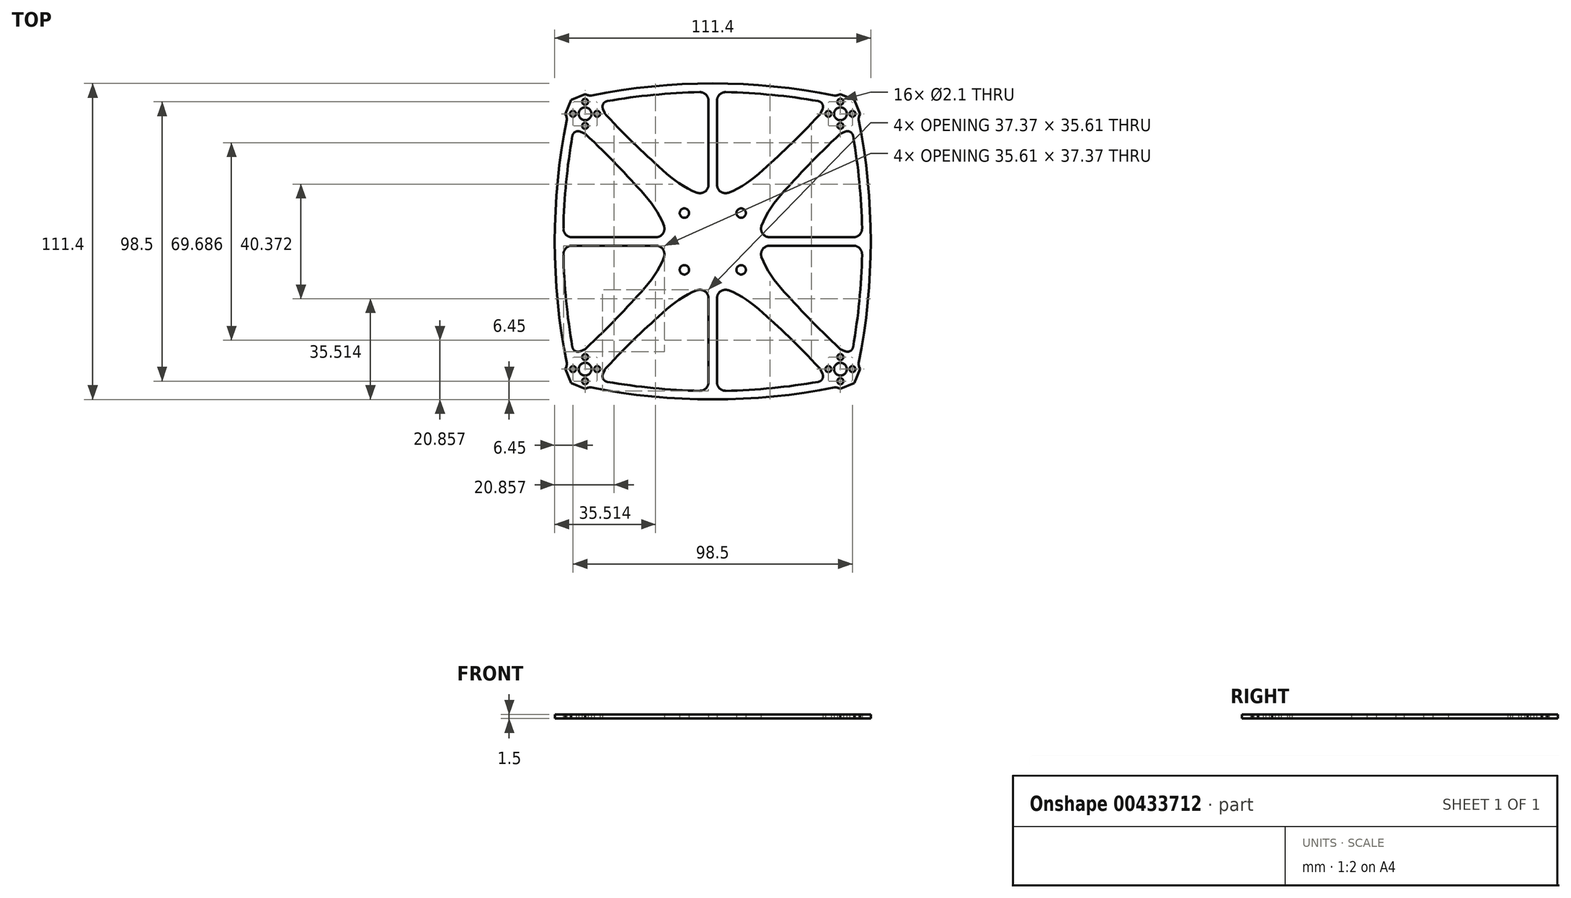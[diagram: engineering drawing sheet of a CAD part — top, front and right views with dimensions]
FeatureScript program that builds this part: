
annotation { "Feature Type Name" : "Feature", "Feature Type Description" : "" }
export const myFeature = defineFeature(function(context is Context, id is Id, definition is map)
    precondition{}
    {
        {
            var Q0;
            Q0=qCreatedBy(makeId("Top.planeOp"),FACE);
            var sketch = newSketch(context, id + "F0", { "sketchPlane" : qUnion([Q0])});
            skLineSegment(sketch, "E0.bottom", {"start": v(45, 45) * mm, "end": v(-45, 45) * mm, "construction": true});
            skLineSegment(sketch, "E0.top", {"start": v(45, -45) * mm, "end": v(-45, -45) * mm, "construction": true});
            skLineSegment(sketch, "E0.left", {"start": v(45, 45) * mm, "end": v(45, -45) * mm, "construction": true});
            skLineSegment(sketch, "E0.right", {"start": v(-45, 45) * mm, "end": v(-45, -45) * mm, "construction": true});
            skPoint(sketch, "E0.middle", {"position": v(0, 0) * mm});
            skLineSegment(sketch, "E1.bottom", {"start": v(10, -10) * mm, "end": v(-10, -10) * mm, "construction": true});
            skLineSegment(sketch, "E1.top", {"start": v(10, 10) * mm, "end": v(-10, 10) * mm, "construction": true});
            skLineSegment(sketch, "E1.left", {"start": v(10, -10) * mm, "end": v(10, 10) * mm, "construction": true});
            skLineSegment(sketch, "E1.right", {"start": v(-10, -10) * mm, "end": v(-10, 10) * mm, "construction": true});
            skCircle(sketch, "E2", {"center": v(45, 45) * mm, "radius": 4.25 * mm, "construction": true});
            skLineSegment(sketch, "E3", {"start": v(-45, 0) * mm, "end": v(45, 0) * mm, "construction": true});
            skLineSegment(sketch, "E4", {"start": v(0, 45) * mm, "end": v(0, -45) * mm, "construction": true});
            skLineSegment(sketch, "E5", {"start": v(0, 0) * mm, "end": v(45, 45) * mm, "construction": true});
            skCircle(sketch, "E6", {"center": v(45, 40.75) * mm, "radius": 1.05 * mm, "construction": true});
            skLineSegment(sketch, "E7", {"start": v(45, 45) * mm, "end": v(56.69, 33.31) * mm, "construction": true});
            skCircle(sketch, "E8.MirrorC", {"center": v(40.75, 45) * mm, "radius": 1.05 * mm, "construction": true});
            skCircle(sketch, "E9.MirrorC", {"center": v(49.25, 45) * mm, "radius": 1.05 * mm, "construction": true});
            skCircle(sketch, "E10.MirrorC", {"center": v(45, 49.25) * mm, "radius": 1.05 * mm, "construction": true});
            skCircle(sketch, "E11", {"center": v(45, 45) * mm, "radius": 6.8 * mm, "construction": true});
            skCircle(sketch, "E12.MirrorC", {"center": v(40.75, -45) * mm, "radius": 1.05 * mm, "construction": true});
            skCircle(sketch, "E13.MirrorC", {"center": v(45, -49.25) * mm, "radius": 1.05 * mm, "construction": true});
            skCircle(sketch, "E14.MirrorC", {"center": v(45, -40.75) * mm, "radius": 1.05 * mm, "construction": true});
            skCircle(sketch, "E15.MirrorC", {"center": v(45, -45) * mm, "radius": 4.25 * mm, "construction": true});
            skCircle(sketch, "E16.MirrorC", {"center": v(49.25, -45) * mm, "radius": 1.05 * mm, "construction": true});
            skCircle(sketch, "E17.MirrorC", {"center": v(45, -45) * mm, "radius": 6.8 * mm, "construction": true});
            skCircle(sketch, "E18.MirrorC", {"center": v(-45, 49.25) * mm, "radius": 1.05 * mm, "construction": true});
            skCircle(sketch, "E19.MirrorC", {"center": v(-45, -49.25) * mm, "radius": 1.05 * mm, "construction": true});
            skCircle(sketch, "E20.MirrorC", {"center": v(-45, -40.75) * mm, "radius": 1.05 * mm, "construction": true});
            skCircle(sketch, "E21.MirrorC", {"center": v(-49.25, -45) * mm, "radius": 1.05 * mm, "construction": true});
            skCircle(sketch, "E22.MirrorC", {"center": v(-49.25, 45) * mm, "radius": 1.05 * mm, "construction": true});
            skCircle(sketch, "E23.MirrorC", {"center": v(-40.75, 45) * mm, "radius": 1.05 * mm, "construction": true});
            skCircle(sketch, "E24.MirrorC", {"center": v(-40.75, -45) * mm, "radius": 1.05 * mm, "construction": true});
            skCircle(sketch, "E25.MirrorC", {"center": v(-45, 40.75) * mm, "radius": 1.05 * mm, "construction": true});
            skCircle(sketch, "E26.MirrorC", {"center": v(-45, -45) * mm, "radius": 4.25 * mm, "construction": true});
            skCircle(sketch, "E27.MirrorC", {"center": v(-45, 45) * mm, "radius": 6.8 * mm, "construction": true});
            skCircle(sketch, "E28.MirrorC", {"center": v(-45, -45) * mm, "radius": 6.8 * mm, "construction": true});
            skCircle(sketch, "E29.MirrorC", {"center": v(-45, 45) * mm, "radius": 4.25 * mm, "construction": true});
            skSolve(sketch);
        }
        {
            var Q0;
            Q0=qCreatedBy(makeId("Top.planeOp"),FACE);
            var sketch = newSketch(context, id + "F1", { "sketchPlane" : qUnion([Q0])});
            skCircle(sketch, "E30", {"center": v(10, 10) * mm, "radius": 1.65 * mm});
            skCircle(sketch, "E31", {"center": v(40.75, 45) * mm, "radius": 1.05 * mm});
            skCircle(sketch, "E32.MirrorC", {"center": v(45, 40.75) * mm, "radius": 1.05 * mm});
            skCircle(sketch, "E33.MirrorC", {"center": v(49.25, 45) * mm, "radius": 1.05 * mm});
            skCircle(sketch, "E34.MirrorC", {"center": v(45, 49.25) * mm, "radius": 1.05 * mm});
            skCircle(sketch, "E35", {"center": v(45, 45) * mm, "radius": 2.25 * mm});
            skCircle(sketch, "E36.cCircle", {"center": v(45, 45) * mm, "radius": 6.47 * mm, "construction": true});
            skLineSegment(sketch, "E36.0", {"start": v(52, 45) * mm, "end": v(51.6, 44.02) * mm});
            skLineSegment(sketch, "E36.1", {"start": v(47.47, 39.03) * mm, "end": v(45, 38) * mm});
            skLineSegment(sketch, "E36.4", {"start": v(38.14, 45.34) * mm, "end": v(38.72, 46.74) * mm});
            skLineSegment(sketch, "E36.5", {"start": v(44.02, 51.6) * mm, "end": v(45, 52) * mm});
            skLineSegment(sketch, "E36.6", {"start": v(45, 52) * mm, "end": v(49.95, 49.95) * mm});
            skLineSegment(sketch, "E36.7", {"start": v(49.95, 49.95) * mm, "end": v(52, 45) * mm});
            skPoint(sketch, "E36.0.midPoint", {"position": v(50.97, 42.53) * mm});
            skFitSpline(sketch, "E37", {"points": [v(38, 45) * mm, v(19.97, 27.24) * mm, v(0, 16.2) * mm], "startDerivative": vector(-40.7, -43.47) * mm, "endDerivative": vector(-49.26, -1.01) * mm});
            skLineSegment(sketch, "E38", {"start": v(0, 16.2) * mm, "end": v(-10.4, 16.2) * mm, "construction": true});
            skFitSpline(sketch, "E39.MirrorCS", {"points": [v(45, 38) * mm, v(27.24, 19.97) * mm, v(16.2, 0) * mm], "startDerivative": vector(-43.47, -40.7) * mm, "endDerivative": vector(-1.01, -49.26) * mm});
            skArc(sketch, "E40", {"start": v(49.95, 49.95) * mm, "mid": v(49.4, 50.08) * mm, "end": v(48.84, 50.2) * mm});
            skArc(sketch, "E41.0", {"start": v(37.22, 49.48) * mm, "mid": v(20.95, 51.68) * mm, "end": v(4.56, 52.65) * mm});
            skLineSegment(sketch, "E42", {"start": v(0, 55.7) * mm, "end": v(-9.83, 55.7) * mm, "construction": true});
            skArc(sketch, "E43.trimOffspring", {"start": v(42.86, 51.48) * mm, "mid": v(21.53, 54.64) * mm, "end": v(0, 55.7) * mm});
            skPoint(sketch, "E44.orphan", {"position": v(40.05, 49.95) * mm});
            skPoint(sketch, "E45.visualSharp", {"position": v(39.67, 49.04) * mm});
            skArc(sketch, "E45.filletArc", {"start": v(38.72, 46.74) * mm, "mid": v(38.63, 48.47) * mm, "end": v(37.22, 49.48) * mm});
            skPoint(sketch, "E46.visualSharp", {"position": v(43.46, 51.36) * mm});
            skArc(sketch, "E46.filletArc", {"start": v(42.86, 51.48) * mm, "mid": v(43.45, 51.45) * mm, "end": v(44.02, 51.6) * mm});
            skArc(sketch, "E47.filletArc", {"start": v(37.75, 44.73) * mm, "mid": v(37.97, 45.02) * mm, "end": v(38.14, 45.34) * mm});
            skArc(sketch, "E48.MirrorCS", {"start": v(49.48, 37.22) * mm, "mid": v(51.68, 20.95) * mm, "end": v(52.65, 4.56) * mm});
            skArc(sketch, "E49.MirrorCS", {"start": v(51.48, 42.86) * mm, "mid": v(54.64, 21.53) * mm, "end": v(55.7, 0) * mm});
            skArc(sketch, "E50.MirrorCS", {"start": v(46.74, 38.72) * mm, "mid": v(48.47, 38.63) * mm, "end": v(49.48, 37.22) * mm});
            skArc(sketch, "E51.MirrorCS", {"start": v(51.48, 42.86) * mm, "mid": v(51.45, 43.45) * mm, "end": v(51.6, 44.02) * mm});
            skPoint(sketch, "E52.orphan", {"position": v(49.95, 40.05) * mm});
            skLineSegment(sketch, "E53", {"start": v(1.5, 49.65) * mm, "end": v(1.5, 20.03) * mm});
            skPoint(sketch, "E54.orphan", {"position": v(0, 52.7) * mm});
            skPoint(sketch, "E55.visualSharp", {"position": v(1.5, 16.3) * mm});
            skArc(sketch, "E55.filletArc", {"start": v(1.5, 20.03) * mm, "mid": v(2.75, 17.59) * mm, "end": v(5.46, 17.19) * mm});
            skPoint(sketch, "E56.visualSharp", {"position": v(1.5, 52.69) * mm});
            skArc(sketch, "E56.filletArc", {"start": v(4.56, 52.65) * mm, "mid": v(2.4, 51.8) * mm, "end": v(1.5, 49.65) * mm});
            skLineSegment(sketch, "E57.MirrorCS", {"start": v(49.65, 1.5) * mm, "end": v(20.03, 1.5) * mm});
            skArc(sketch, "E58.MirrorCS", {"start": v(20.03, 1.5) * mm, "mid": v(17.59, 2.75) * mm, "end": v(17.19, 5.46) * mm});
            skArc(sketch, "E59.MirrorCS", {"start": v(52.65, 4.56) * mm, "mid": v(51.8, 2.4) * mm, "end": v(49.65, 1.5) * mm});
            skPoint(sketch, "E60.orphan", {"position": v(52.7, 0) * mm});
            skArc(sketch, "E61.MirrorCS", {"start": v(37.75, -44.73) * mm, "mid": v(37.97, -45.02) * mm, "end": v(38.14, -45.34) * mm});
            skLineSegment(sketch, "E62.MirrorCS", {"start": v(38.14, -45.34) * mm, "end": v(38.72, -46.74) * mm});
            skCircle(sketch, "E63.MirrorC", {"center": v(45, -40.75) * mm, "radius": 1.05 * mm});
            skArc(sketch, "E64.MirrorCS", {"start": v(49.95, -49.95) * mm, "mid": v(49.4, -50.08) * mm, "end": v(48.84, -50.2) * mm});
            skLineSegment(sketch, "E65.MirrorCS", {"start": v(44.02, -51.6) * mm, "end": v(45, -52) * mm});
            skLineSegment(sketch, "E66.MirrorCS", {"start": v(45, -52) * mm, "end": v(49.95, -49.95) * mm});
            skLineSegment(sketch, "E67.MirrorCS", {"start": v(47.47, -39.03) * mm, "end": v(45, -38) * mm});
            skArc(sketch, "E68.MirrorCS", {"start": v(51.48, -42.86) * mm, "mid": v(51.45, -43.45) * mm, "end": v(51.6, -44.02) * mm});
            skArc(sketch, "E69.MirrorCS", {"start": v(42.86, -51.48) * mm, "mid": v(43.45, -51.45) * mm, "end": v(44.02, -51.6) * mm});
            skLineSegment(sketch, "E70.MirrorCS", {"start": v(52, -45) * mm, "end": v(51.6, -44.02) * mm});
            skArc(sketch, "E71.MirrorCS", {"start": v(38.72, -46.74) * mm, "mid": v(38.63, -48.47) * mm, "end": v(37.22, -49.48) * mm});
            skArc(sketch, "E72.MirrorCS", {"start": v(4.56, -52.65) * mm, "mid": v(2.4, -51.8) * mm, "end": v(1.5, -49.65) * mm});
            skArc(sketch, "E73.MirrorCS", {"start": v(46.74, -38.72) * mm, "mid": v(48.47, -38.63) * mm, "end": v(49.48, -37.22) * mm});
            skArc(sketch, "E74.MirrorCS", {"start": v(52.65, -4.56) * mm, "mid": v(51.8, -2.4) * mm, "end": v(49.65, -1.5) * mm});
            skCircle(sketch, "E75.MirrorC", {"center": v(40.75, -45) * mm, "radius": 1.05 * mm});
            skPoint(sketch, "E76.MirrorP", {"position": v(38, -45) * mm});
            skCircle(sketch, "E77.MirrorC", {"center": v(49.25, -45) * mm, "radius": 1.05 * mm});
            skArc(sketch, "E78.MirrorCS", {"start": v(1.5, -20.03) * mm, "mid": v(2.75, -17.59) * mm, "end": v(5.46, -17.19) * mm});
            skCircle(sketch, "E79.MirrorC", {"center": v(45, -45) * mm, "radius": 2.25 * mm});
            skCircle(sketch, "E80.MirrorC", {"center": v(45, -49.25) * mm, "radius": 1.05 * mm});
            skArc(sketch, "E81.MirrorCS", {"start": v(20.03, -1.5) * mm, "mid": v(17.59, -2.75) * mm, "end": v(17.19, -5.46) * mm});
            skCircle(sketch, "E82.MirrorC", {"center": v(10, -10) * mm, "radius": 1.65 * mm});
            skLineSegment(sketch, "E83.MirrorCS", {"start": v(49.95, -49.95) * mm, "end": v(52, -45) * mm});
            skLineSegment(sketch, "E84.MirrorCS", {"start": v(0, -16.2) * mm, "end": v(-10.4, -16.2) * mm, "construction": true});
            skFitSpline(sketch, "E85.MirrorCS", {"points": [v(38, -45) * mm, v(19.97, -27.24) * mm, v(0, -16.2) * mm], "startDerivative": vector(-40.7, 43.47) * mm, "endDerivative": vector(-49.26, 1.01) * mm});
            skArc(sketch, "E86.MirrorCS", {"start": v(42.86, -51.48) * mm, "mid": v(21.53, -54.64) * mm, "end": v(0, -55.7) * mm});
            skLineSegment(sketch, "E87.MirrorCS", {"start": v(1.5, -49.65) * mm, "end": v(1.5, -20.03) * mm});
            skFitSpline(sketch, "E88.MirrorCS", {"points": [v(45, -38) * mm, v(27.24, -19.97) * mm, v(16.2, 0) * mm], "startDerivative": vector(-43.47, 40.7) * mm, "endDerivative": vector(-1.01, 49.26) * mm});
            skPoint(sketch, "E89.MirrorP", {"position": v(43.46, -51.36) * mm});
            skArc(sketch, "E90.MirrorCS", {"start": v(51.48, -42.86) * mm, "mid": v(54.64, -21.53) * mm, "end": v(55.7, 0) * mm});
            skPoint(sketch, "E91.MirrorP", {"position": v(39.67, -49.04) * mm});
            skPoint(sketch, "E92.MirrorP", {"position": v(0, -52.7) * mm});
            skPoint(sketch, "E93.MirrorP", {"position": v(1.5, -16.3) * mm});
            skLineSegment(sketch, "E94.MirrorCS", {"start": v(49.65, -1.5) * mm, "end": v(20.03, -1.5) * mm});
            skArc(sketch, "E95.MirrorCS", {"start": v(49.48, -37.22) * mm, "mid": v(51.68, -20.95) * mm, "end": v(52.65, -4.56) * mm});
            skPoint(sketch, "E96.MirrorP", {"position": v(1.5, -52.69) * mm});
            skCircle(sketch, "E97.MirrorC", {"center": v(45, -45) * mm, "radius": 6.47 * mm, "construction": true});
            skArc(sketch, "E98.MirrorCS", {"start": v(37.22, -49.48) * mm, "mid": v(20.95, -51.68) * mm, "end": v(4.56, -52.65) * mm});
            skPoint(sketch, "E99.MirrorP", {"position": v(50.97, -42.53) * mm});
            skLineSegment(sketch, "E100.MirrorCS", {"start": v(0, -55.7) * mm, "end": v(-9.83, -55.7) * mm, "construction": true});
            skPoint(sketch, "E101.MirrorP", {"position": v(40.05, -49.95) * mm});
            skPoint(sketch, "E102.MirrorP", {"position": v(49.95, -40.05) * mm});
            skArc(sketch, "E103.MirrorCS", {"start": v(-37.75, 44.73) * mm, "mid": v(-37.97, 45.02) * mm, "end": v(-38.14, 45.34) * mm});
            skLineSegment(sketch, "E104.MirrorCS", {"start": v(-38.14, 45.34) * mm, "end": v(-38.72, 46.74) * mm});
            skLineSegment(sketch, "E105.MirrorCS", {"start": v(-44.02, 51.6) * mm, "end": v(-45, 52) * mm});
            skLineSegment(sketch, "E106.MirrorCS", {"start": v(-38.14, -45.34) * mm, "end": v(-38.72, -46.74) * mm});
            skCircle(sketch, "E107.MirrorC", {"center": v(-45, -40.75) * mm, "radius": 1.05 * mm});
            skArc(sketch, "E108.MirrorCS", {"start": v(-42.86, 51.48) * mm, "mid": v(-43.45, 51.45) * mm, "end": v(-44.02, 51.6) * mm});
            skCircle(sketch, "E109.MirrorC", {"center": v(-45, 40.75) * mm, "radius": 1.05 * mm});
            skArc(sketch, "E110.MirrorCS", {"start": v(-49.95, 49.95) * mm, "mid": v(-49.4, 50.08) * mm, "end": v(-48.84, 50.2) * mm});
            skArc(sketch, "E111.MirrorCS", {"start": v(-37.75, -44.73) * mm, "mid": v(-37.97, -45.02) * mm, "end": v(-38.14, -45.34) * mm});
            skLineSegment(sketch, "E112.MirrorCS", {"start": v(-44.02, -51.6) * mm, "end": v(-45, -52) * mm});
            skLineSegment(sketch, "E113.MirrorCS", {"start": v(-52, 45) * mm, "end": v(-51.6, 44.02) * mm});
            skLineSegment(sketch, "E114.MirrorCS", {"start": v(-52, -45) * mm, "end": v(-51.6, -44.02) * mm});
            skArc(sketch, "E115.MirrorCS", {"start": v(-42.86, -51.48) * mm, "mid": v(-43.45, -51.45) * mm, "end": v(-44.02, -51.6) * mm});
            skArc(sketch, "E116.MirrorCS", {"start": v(-49.95, -49.95) * mm, "mid": v(-49.4, -50.08) * mm, "end": v(-48.84, -50.2) * mm});
            skArc(sketch, "E117.MirrorCS", {"start": v(-51.48, 42.86) * mm, "mid": v(-51.45, 43.45) * mm, "end": v(-51.6, 44.02) * mm});
            skArc(sketch, "E118.MirrorCS", {"start": v(-38.72, 46.74) * mm, "mid": v(-38.63, 48.47) * mm, "end": v(-37.22, 49.48) * mm});
            skLineSegment(sketch, "E119.MirrorCS", {"start": v(-49.95, 49.95) * mm, "end": v(-52, 45) * mm});
            skLineSegment(sketch, "E120.MirrorCS", {"start": v(-47.47, -39.03) * mm, "end": v(-45, -38) * mm});
            skArc(sketch, "E121.MirrorCS", {"start": v(-51.48, -42.86) * mm, "mid": v(-51.45, -43.45) * mm, "end": v(-51.6, -44.02) * mm});
            skArc(sketch, "E122.MirrorCS", {"start": v(-46.74, -38.72) * mm, "mid": v(-48.47, -38.63) * mm, "end": v(-49.48, -37.22) * mm});
            skArc(sketch, "E123.MirrorCS", {"start": v(-38.72, -46.74) * mm, "mid": v(-38.63, -48.47) * mm, "end": v(-37.22, -49.48) * mm});
            skArc(sketch, "E124.MirrorCS", {"start": v(-20.03, 1.5) * mm, "mid": v(-17.59, 2.75) * mm, "end": v(-17.19, 5.46) * mm});
            skLineSegment(sketch, "E125.MirrorCS", {"start": v(-47.47, 39.03) * mm, "end": v(-45, 38) * mm});
            skArc(sketch, "E126.MirrorCS", {"start": v(-52.65, -4.56) * mm, "mid": v(-51.8, -2.4) * mm, "end": v(-49.65, -1.5) * mm});
            skArc(sketch, "E127.MirrorCS", {"start": v(-46.74, 38.72) * mm, "mid": v(-48.47, 38.63) * mm, "end": v(-49.48, 37.22) * mm});
            skLineSegment(sketch, "E128.MirrorCS", {"start": v(-49.95, -49.95) * mm, "end": v(-52, -45) * mm});
            skArc(sketch, "E129.MirrorCS", {"start": v(-20.03, -1.5) * mm, "mid": v(-17.59, -2.75) * mm, "end": v(-17.19, -5.46) * mm});
            skArc(sketch, "E130.MirrorCS", {"start": v(-52.65, 4.56) * mm, "mid": v(-51.8, 2.4) * mm, "end": v(-49.65, 1.5) * mm});
            skCircle(sketch, "E131.MirrorC", {"center": v(-45, -45) * mm, "radius": 2.25 * mm});
            skCircle(sketch, "E132.MirrorC", {"center": v(-45, 49.25) * mm, "radius": 1.05 * mm});
            skArc(sketch, "E133.MirrorCS", {"start": v(-1.5, 20.03) * mm, "mid": v(-2.75, 17.59) * mm, "end": v(-5.46, 17.19) * mm});
            skPoint(sketch, "E134.MirrorP", {"position": v(-52.7, 0) * mm});
            skCircle(sketch, "E135.MirrorC", {"center": v(-10, 10) * mm, "radius": 1.65 * mm});
            skArc(sketch, "E136.MirrorCS", {"start": v(-4.56, 52.65) * mm, "mid": v(-2.4, 51.8) * mm, "end": v(-1.5, 49.65) * mm});
            skPoint(sketch, "E137.MirrorP", {"position": v(-38, 45) * mm});
            skCircle(sketch, "E138.MirrorC", {"center": v(-45, -49.25) * mm, "radius": 1.05 * mm});
            skArc(sketch, "E139.MirrorCS", {"start": v(-4.56, -52.65) * mm, "mid": v(-2.4, -51.8) * mm, "end": v(-1.5, -49.65) * mm});
            skCircle(sketch, "E140.MirrorC", {"center": v(-45, 45) * mm, "radius": 2.25 * mm});
            skArc(sketch, "E141.MirrorCS", {"start": v(-1.5, -20.03) * mm, "mid": v(-2.75, -17.59) * mm, "end": v(-5.46, -17.19) * mm});
            skCircle(sketch, "E142.MirrorC", {"center": v(-10, -10) * mm, "radius": 1.65 * mm});
            skLineSegment(sketch, "E143.MirrorCS", {"start": v(-45, 52) * mm, "end": v(-49.95, 49.95) * mm});
            skLineSegment(sketch, "E144.MirrorCS", {"start": v(-45, -52) * mm, "end": v(-49.95, -49.95) * mm});
            skCircle(sketch, "E145.MirrorC", {"center": v(-40.75, 45) * mm, "radius": 1.05 * mm});
            skCircle(sketch, "E146.MirrorC", {"center": v(-49.25, 45) * mm, "radius": 1.05 * mm});
            skCircle(sketch, "E147.MirrorC", {"center": v(-40.75, -45) * mm, "radius": 1.05 * mm});
            skCircle(sketch, "E148.MirrorC", {"center": v(-49.25, -45) * mm, "radius": 1.05 * mm});
            skPoint(sketch, "E149.MirrorP", {"position": v(-16.2, 0) * mm});
            skPoint(sketch, "E150.MirrorP", {"position": v(-1.5, -52.69) * mm});
            skPoint(sketch, "E151.MirrorP", {"position": v(-49.95, 40.05) * mm});
            skLineSegment(sketch, "E152.MirrorCS", {"start": v(-49.65, -1.5) * mm, "end": v(-20.03, -1.5) * mm});
            skCircle(sketch, "E153.MirrorC", {"center": v(-45, 45) * mm, "radius": 6.47 * mm, "construction": true});
            skArc(sketch, "E154.MirrorCS", {"start": v(-49.48, -37.22) * mm, "mid": v(-51.68, -20.95) * mm, "end": v(-52.65, -4.56) * mm});
            skPoint(sketch, "E155.MirrorP", {"position": v(-1.5, -16.3) * mm});
            skLineSegment(sketch, "E156.MirrorCS", {"start": v(-1.5, -49.65) * mm, "end": v(-1.5, -20.03) * mm});
            skFitSpline(sketch, "E157.MirrorCS", {"points": [v(-38, -45) * mm, v(-19.97, -27.24) * mm, v(0, -16.2) * mm], "startDerivative": vector(40.7, 43.47) * mm, "endDerivative": vector(49.26, 1.01) * mm});
            skArc(sketch, "E158.MirrorCS", {"start": v(-42.86, 51.48) * mm, "mid": v(-21.53, 54.64) * mm, "end": v(0, 55.7) * mm});
            skFitSpline(sketch, "E159.MirrorCS", {"points": [v(-45, 38) * mm, v(-27.24, 19.97) * mm, v(-16.2, 0) * mm], "startDerivative": vector(43.47, -40.7) * mm, "endDerivative": vector(1.01, -49.26) * mm});
            skPoint(sketch, "E160.MirrorP", {"position": v(-39.67, -49.04) * mm});
            skFitSpline(sketch, "E161.MirrorCS", {"points": [v(-38, 45) * mm, v(-19.97, 27.24) * mm, v(0, 16.2) * mm], "startDerivative": vector(40.7, -43.47) * mm, "endDerivative": vector(49.26, -1.01) * mm});
            skFitSpline(sketch, "E162.MirrorCS", {"points": [v(-45, -38) * mm, v(-27.24, -19.97) * mm, v(-16.2, 0) * mm], "startDerivative": vector(43.47, 40.7) * mm, "endDerivative": vector(1.01, 49.26) * mm});
            skLineSegment(sketch, "E163.MirrorCS", {"start": v(-1.5, 49.65) * mm, "end": v(-1.5, 20.03) * mm});
            skPoint(sketch, "E164.MirrorP", {"position": v(-43.46, 51.36) * mm});
            skPoint(sketch, "E165.MirrorP", {"position": v(-43.46, -51.36) * mm});
            skArc(sketch, "E166.MirrorCS", {"start": v(-42.86, -51.48) * mm, "mid": v(-21.53, -54.64) * mm, "end": v(0, -55.7) * mm});
            skPoint(sketch, "E167.MirrorP", {"position": v(-50.97, 42.53) * mm});
            skLineSegment(sketch, "E168.MirrorCS", {"start": v(-49.65, 1.5) * mm, "end": v(-20.03, 1.5) * mm});
            skPoint(sketch, "E169.MirrorP", {"position": v(-49.95, -40.05) * mm});
            skPoint(sketch, "E170.MirrorP", {"position": v(-39.67, 49.04) * mm});
            skArc(sketch, "E171.MirrorCS", {"start": v(-49.48, 37.22) * mm, "mid": v(-51.68, 20.95) * mm, "end": v(-52.65, 4.56) * mm});
            skCircle(sketch, "E172.MirrorC", {"center": v(-45, -45) * mm, "radius": 6.47 * mm, "construction": true});
            skPoint(sketch, "E173.MirrorP", {"position": v(-40.05, -49.95) * mm});
            skArc(sketch, "E174.MirrorCS", {"start": v(-37.22, 49.48) * mm, "mid": v(-20.95, 51.68) * mm, "end": v(-4.56, 52.65) * mm});
            skArc(sketch, "E175.MirrorCS", {"start": v(-37.22, -49.48) * mm, "mid": v(-20.95, -51.68) * mm, "end": v(-4.56, -52.65) * mm});
            skPoint(sketch, "E176.MirrorP", {"position": v(-40.05, 49.95) * mm});
            skArc(sketch, "E177.MirrorCS", {"start": v(-51.48, 42.86) * mm, "mid": v(-54.64, 21.53) * mm, "end": v(-55.7, 0) * mm});
            skPoint(sketch, "E178.MirrorP", {"position": v(-1.5, 16.3) * mm});
            skPoint(sketch, "E179.MirrorP", {"position": v(-50.97, -42.53) * mm});
            skPoint(sketch, "E180.MirrorP", {"position": v(-1.5, 52.69) * mm});
            skArc(sketch, "E181.MirrorCS", {"start": v(-51.48, -42.86) * mm, "mid": v(-54.64, -21.53) * mm, "end": v(-55.7, 0) * mm});
            skSolve(sketch);
        }
        {
            var Q0;
            Q0=makeQuery(id+"F1.imprint","IMPRINT",FACE,{"disambiguationData":[TD([[makeQuery(id+"F1.imprint","IMPRINT",EDGE,{"derivedFrom":sQuery(id+"F1.wireOp",EDGE,"E30")}),-1.0]])]});
            extrude(context, id + "F2", {"entities" : qUnion([Q0]), "depth" : 1.5 * mm});
        }
        {
            var Q0;
            Q0=makeQuery(id+"F2.opExtrude","CAP_FACE",FACE,{"disambiguationData":[OSD([sQuery(id+"F1.wireOp",EDGE,"E30"),sQuery(id+"F1.wireOp",EDGE,"E31"),sQuery(id+"F1.wireOp",EDGE,"E32.MirrorC"),sQuery(id+"F1.wireOp",EDGE,"E33.MirrorC"),sQuery(id+"F1.wireOp",EDGE,"E34.MirrorC"),sQuery(id+"F1.wireOp",EDGE,"E35"),sQuery(id+"F1.wireOp",EDGE,"E36.0"),sQuery(id+"F1.wireOp",EDGE,"E36.1"),sQuery(id+"F1.wireOp",EDGE,"E36.4"),sQuery(id+"F1.wireOp",EDGE,"E36.5"),sQuery(id+"F1.wireOp",EDGE,"E36.6"),sQuery(id+"F1.wireOp",EDGE,"E36.7"),sQuery(id+"F1.wireOp",EDGE,"E37"),sQuery(id+"F1.wireOp",EDGE,"E39.MirrorCS"),sQuery(id+"F1.wireOp",EDGE,"E41.0"),sQuery(id+"F1.wireOp",EDGE,"E43.trimOffspring"),sQuery(id+"F1.wireOp",EDGE,"E45.filletArc"),sQuery(id+"F1.wireOp",EDGE,"E46.filletArc"),sQuery(id+"F1.wireOp",EDGE,"E47.filletArc"),sQuery(id+"F1.wireOp",EDGE,"E48.MirrorCS"),sQuery(id+"F1.wireOp",EDGE,"E49.MirrorCS"),sQuery(id+"F1.wireOp",EDGE,"E50.MirrorCS"),sQuery(id+"F1.wireOp",EDGE,"E51.MirrorCS"),sQuery(id+"F1.wireOp",EDGE,"E53"),sQuery(id+"F1.wireOp",EDGE,"E55.filletArc"),sQuery(id+"F1.wireOp",EDGE,"E56.filletArc"),sQuery(id+"F1.wireOp",EDGE,"E57.MirrorCS"),sQuery(id+"F1.wireOp",EDGE,"E58.MirrorCS"),sQuery(id+"F1.wireOp",EDGE,"E59.MirrorCS"),sQuery(id+"F1.wireOp",EDGE,"E61.MirrorCS"),sQuery(id+"F1.wireOp",EDGE,"E62.MirrorCS"),sQuery(id+"F1.wireOp",EDGE,"E65.MirrorCS"),sQuery(id+"F1.wireOp",EDGE,"E66.MirrorCS"),sQuery(id+"F1.wireOp",EDGE,"E67.MirrorCS"),sQuery(id+"F1.wireOp",EDGE,"E63.MirrorC"),sQuery(id+"F1.wireOp",EDGE,"E68.MirrorCS"),sQuery(id+"F1.wireOp",EDGE,"E69.MirrorCS"),sQuery(id+"F1.wireOp",EDGE,"E70.MirrorCS"),sQuery(id+"F1.wireOp",EDGE,"E71.MirrorCS"),sQuery(id+"F1.wireOp",EDGE,"E72.MirrorCS"),sQuery(id+"F1.wireOp",EDGE,"E73.MirrorCS"),sQuery(id+"F1.wireOp",EDGE,"E74.MirrorCS"),sQuery(id+"F1.wireOp",EDGE,"E75.MirrorC"),sQuery(id+"F1.wireOp",EDGE,"E77.MirrorC"),sQuery(id+"F1.wireOp",EDGE,"E78.MirrorCS"),sQuery(id+"F1.wireOp",EDGE,"E79.MirrorC"),sQuery(id+"F1.wireOp",EDGE,"E80.MirrorC"),sQuery(id+"F1.wireOp",EDGE,"E81.MirrorCS"),sQuery(id+"F1.wireOp",EDGE,"E82.MirrorC"),sQuery(id+"F1.wireOp",EDGE,"E83.MirrorCS"),sQuery(id+"F1.wireOp",EDGE,"E85.MirrorCS"),sQuery(id+"F1.wireOp",EDGE,"E86.MirrorCS"),sQuery(id+"F1.wireOp",EDGE,"E87.MirrorCS"),sQuery(id+"F1.wireOp",EDGE,"E88.MirrorCS"),sQuery(id+"F1.wireOp",EDGE,"E90.MirrorCS"),sQuery(id+"F1.wireOp",EDGE,"E94.MirrorCS"),sQuery(id+"F1.wireOp",EDGE,"E95.MirrorCS"),sQuery(id+"F1.wireOp",EDGE,"E98.MirrorCS"),sQuery(id+"F1.wireOp",EDGE,"E103.MirrorCS"),sQuery(id+"F1.wireOp",EDGE,"E104.MirrorCS"),sQuery(id+"F1.wireOp",EDGE,"E105.MirrorCS"),sQuery(id+"F1.wireOp",EDGE,"E106.MirrorCS"),sQuery(id+"F1.wireOp",EDGE,"E108.MirrorCS"),sQuery(id+"F1.wireOp",EDGE,"E111.MirrorCS"),sQuery(id+"F1.wireOp",EDGE,"E112.MirrorCS"),sQuery(id+"F1.wireOp",EDGE,"E113.MirrorCS"),sQuery(id+"F1.wireOp",EDGE,"E114.MirrorCS"),sQuery(id+"F1.wireOp",EDGE,"E115.MirrorCS"),sQuery(id+"F1.wireOp",EDGE,"E117.MirrorCS"),sQuery(id+"F1.wireOp",EDGE,"E118.MirrorCS"),sQuery(id+"F1.wireOp",EDGE,"E119.MirrorCS"),sQuery(id+"F1.wireOp",EDGE,"E109.MirrorC"),sQuery(id+"F1.wireOp",EDGE,"E120.MirrorCS"),sQuery(id+"F1.wireOp",EDGE,"E121.MirrorCS"),sQuery(id+"F1.wireOp",EDGE,"E107.MirrorC"),sQuery(id+"F1.wireOp",EDGE,"E122.MirrorCS"),sQuery(id+"F1.wireOp",EDGE,"E123.MirrorCS"),sQuery(id+"F1.wireOp",EDGE,"E124.MirrorCS"),sQuery(id+"F1.wireOp",EDGE,"E125.MirrorCS"),sQuery(id+"F1.wireOp",EDGE,"E126.MirrorCS"),sQuery(id+"F1.wireOp",EDGE,"E127.MirrorCS"),sQuery(id+"F1.wireOp",EDGE,"E128.MirrorCS"),sQuery(id+"F1.wireOp",EDGE,"E129.MirrorCS"),sQuery(id+"F1.wireOp",EDGE,"E130.MirrorCS"),sQuery(id+"F1.wireOp",EDGE,"E131.MirrorC"),sQuery(id+"F1.wireOp",EDGE,"E132.MirrorC"),sQuery(id+"F1.wireOp",EDGE,"E133.MirrorCS"),sQuery(id+"F1.wireOp",EDGE,"E135.MirrorC"),sQuery(id+"F1.wireOp",EDGE,"E136.MirrorCS"),sQuery(id+"F1.wireOp",EDGE,"E138.MirrorC"),sQuery(id+"F1.wireOp",EDGE,"E139.MirrorCS"),sQuery(id+"F1.wireOp",EDGE,"E140.MirrorC"),sQuery(id+"F1.wireOp",EDGE,"E141.MirrorCS"),sQuery(id+"F1.wireOp",EDGE,"E142.MirrorC"),sQuery(id+"F1.wireOp",EDGE,"E143.MirrorCS"),sQuery(id+"F1.wireOp",EDGE,"E144.MirrorCS"),sQuery(id+"F1.wireOp",EDGE,"E145.MirrorC"),sQuery(id+"F1.wireOp",EDGE,"E146.MirrorC"),sQuery(id+"F1.wireOp",EDGE,"E147.MirrorC"),sQuery(id+"F1.wireOp",EDGE,"E148.MirrorC"),sQuery(id+"F1.wireOp",EDGE,"E152.MirrorCS"),sQuery(id+"F1.wireOp",EDGE,"E154.MirrorCS"),sQuery(id+"F1.wireOp",EDGE,"E156.MirrorCS"),sQuery(id+"F1.wireOp",EDGE,"E157.MirrorCS"),sQuery(id+"F1.wireOp",EDGE,"E158.MirrorCS"),sQuery(id+"F1.wireOp",EDGE,"E159.MirrorCS"),sQuery(id+"F1.wireOp",EDGE,"E161.MirrorCS"),sQuery(id+"F1.wireOp",EDGE,"E162.MirrorCS"),sQuery(id+"F1.wireOp",EDGE,"E163.MirrorCS"),sQuery(id+"F1.wireOp",EDGE,"E166.MirrorCS"),sQuery(id+"F1.wireOp",EDGE,"E168.MirrorCS"),sQuery(id+"F1.wireOp",EDGE,"E171.MirrorCS"),sQuery(id+"F1.wireOp",EDGE,"E174.MirrorCS"),sQuery(id+"F1.wireOp",EDGE,"E175.MirrorCS"),sQuery(id+"F1.wireOp",EDGE,"E177.MirrorCS"),sQuery(id+"F1.wireOp",EDGE,"E181.MirrorCS")])],"isStart":false});
            var sketch = newSketch(context, id + "F3", { "sketchPlane" : qUnion([Q0])});
            skCircle(sketch, "E182.cCircle", {"center": v(-10, 10) * mm, "radius": 2.78 * mm, "construction": true});
            skLineSegment(sketch, "E182.0", {"start": v(-7.11, 9.17) * mm, "end": v(-8.54, 7.37) * mm});
            skLineSegment(sketch, "E182.1", {"start": v(-8.54, 7.37) * mm, "end": v(-10.83, 7.11) * mm});
            skLineSegment(sketch, "E182.2", {"start": v(-10.83, 7.11) * mm, "end": v(-12.63, 8.54) * mm});
            skLineSegment(sketch, "E182.3", {"start": v(-12.63, 8.54) * mm, "end": v(-12.89, 10.83) * mm});
            skLineSegment(sketch, "E182.4", {"start": v(-12.89, 10.83) * mm, "end": v(-11.46, 12.63) * mm});
            skLineSegment(sketch, "E182.5", {"start": v(-11.46, 12.63) * mm, "end": v(-9.17, 12.89) * mm});
            skLineSegment(sketch, "E182.6", {"start": v(-9.17, 12.89) * mm, "end": v(-7.37, 11.46) * mm});
            skLineSegment(sketch, "E182.7", {"start": v(-7.37, 11.46) * mm, "end": v(-7.11, 9.17) * mm});
            skPoint(sketch, "E182.0.midPoint", {"position": v(-7.83, 8.27) * mm});
            skLineSegment(sketch, "E183.0.1.0", {"start": v(-11.46, -7.37) * mm, "end": v(-9.17, -7.11) * mm});
            skCircle(sketch, "E183.0.1.1", {"center": v(-10, -10) * mm, "radius": 2.78 * mm, "construction": true});
            skLineSegment(sketch, "E183.0.1.2", {"start": v(-12.63, -11.46) * mm, "end": v(-12.89, -9.17) * mm});
            skLineSegment(sketch, "E183.0.1.3", {"start": v(-10.83, -12.89) * mm, "end": v(-12.63, -11.46) * mm});
            skPoint(sketch, "E183.0.1.4", {"position": v(-7.83, -11.73) * mm});
            skLineSegment(sketch, "E183.0.1.5", {"start": v(-8.54, -12.63) * mm, "end": v(-10.83, -12.89) * mm});
            skLineSegment(sketch, "E183.0.1.6", {"start": v(-7.37, -8.54) * mm, "end": v(-7.11, -10.83) * mm});
            skLineSegment(sketch, "E183.0.1.7", {"start": v(-9.17, -7.11) * mm, "end": v(-7.37, -8.54) * mm});
            skLineSegment(sketch, "E183.0.1.8", {"start": v(-7.11, -10.83) * mm, "end": v(-8.54, -12.63) * mm});
            skLineSegment(sketch, "E183.0.1.9", {"start": v(-12.89, -9.17) * mm, "end": v(-11.46, -7.37) * mm});
            skLineSegment(sketch, "E183.1.0.0", {"start": v(8.54, 12.63) * mm, "end": v(10.83, 12.89) * mm});
            skCircle(sketch, "E183.1.0.1", {"center": v(10, 10) * mm, "radius": 2.78 * mm, "construction": true});
            skLineSegment(sketch, "E183.1.0.2", {"start": v(7.37, 8.54) * mm, "end": v(7.11, 10.83) * mm});
            skLineSegment(sketch, "E183.1.0.3", {"start": v(9.17, 7.11) * mm, "end": v(7.37, 8.54) * mm});
            skPoint(sketch, "E183.1.0.4", {"position": v(12.17, 8.27) * mm});
            skLineSegment(sketch, "E183.1.0.5", {"start": v(11.46, 7.37) * mm, "end": v(9.17, 7.11) * mm});
            skLineSegment(sketch, "E183.1.0.6", {"start": v(12.63, 11.46) * mm, "end": v(12.89, 9.17) * mm});
            skLineSegment(sketch, "E183.1.0.7", {"start": v(10.83, 12.89) * mm, "end": v(12.63, 11.46) * mm});
            skLineSegment(sketch, "E183.1.0.8", {"start": v(12.89, 9.17) * mm, "end": v(11.46, 7.37) * mm});
            skLineSegment(sketch, "E183.1.0.9", {"start": v(7.11, 10.83) * mm, "end": v(8.54, 12.63) * mm});
            skLineSegment(sketch, "E183.1.1.0", {"start": v(8.54, -7.37) * mm, "end": v(10.83, -7.11) * mm});
            skCircle(sketch, "E183.1.1.1", {"center": v(10, -10) * mm, "radius": 2.78 * mm, "construction": true});
            skLineSegment(sketch, "E183.1.1.2", {"start": v(7.37, -11.46) * mm, "end": v(7.11, -9.17) * mm});
            skLineSegment(sketch, "E183.1.1.3", {"start": v(9.17, -12.89) * mm, "end": v(7.37, -11.46) * mm});
            skPoint(sketch, "E183.1.1.4", {"position": v(12.17, -11.73) * mm});
            skLineSegment(sketch, "E183.1.1.5", {"start": v(11.46, -12.63) * mm, "end": v(9.17, -12.89) * mm});
            skLineSegment(sketch, "E183.1.1.6", {"start": v(12.63, -8.54) * mm, "end": v(12.89, -10.83) * mm});
            skLineSegment(sketch, "E183.1.1.7", {"start": v(10.83, -7.11) * mm, "end": v(12.63, -8.54) * mm});
            skLineSegment(sketch, "E183.1.1.8", {"start": v(12.89, -10.83) * mm, "end": v(11.46, -12.63) * mm});
            skLineSegment(sketch, "E183.1.1.9", {"start": v(7.11, -9.17) * mm, "end": v(8.54, -7.37) * mm});
            skLineSegment(sketch, "E183.direction1", {"start": v(-12.63, 8.54) * mm, "end": v(7.37, 8.54) * mm, "construction": true});
            skLineSegment(sketch, "E183.direction2", {"start": v(-12.63, 8.54) * mm, "end": v(-12.63, -11.46) * mm, "construction": true});
            skSolve(sketch);
        }
    });
